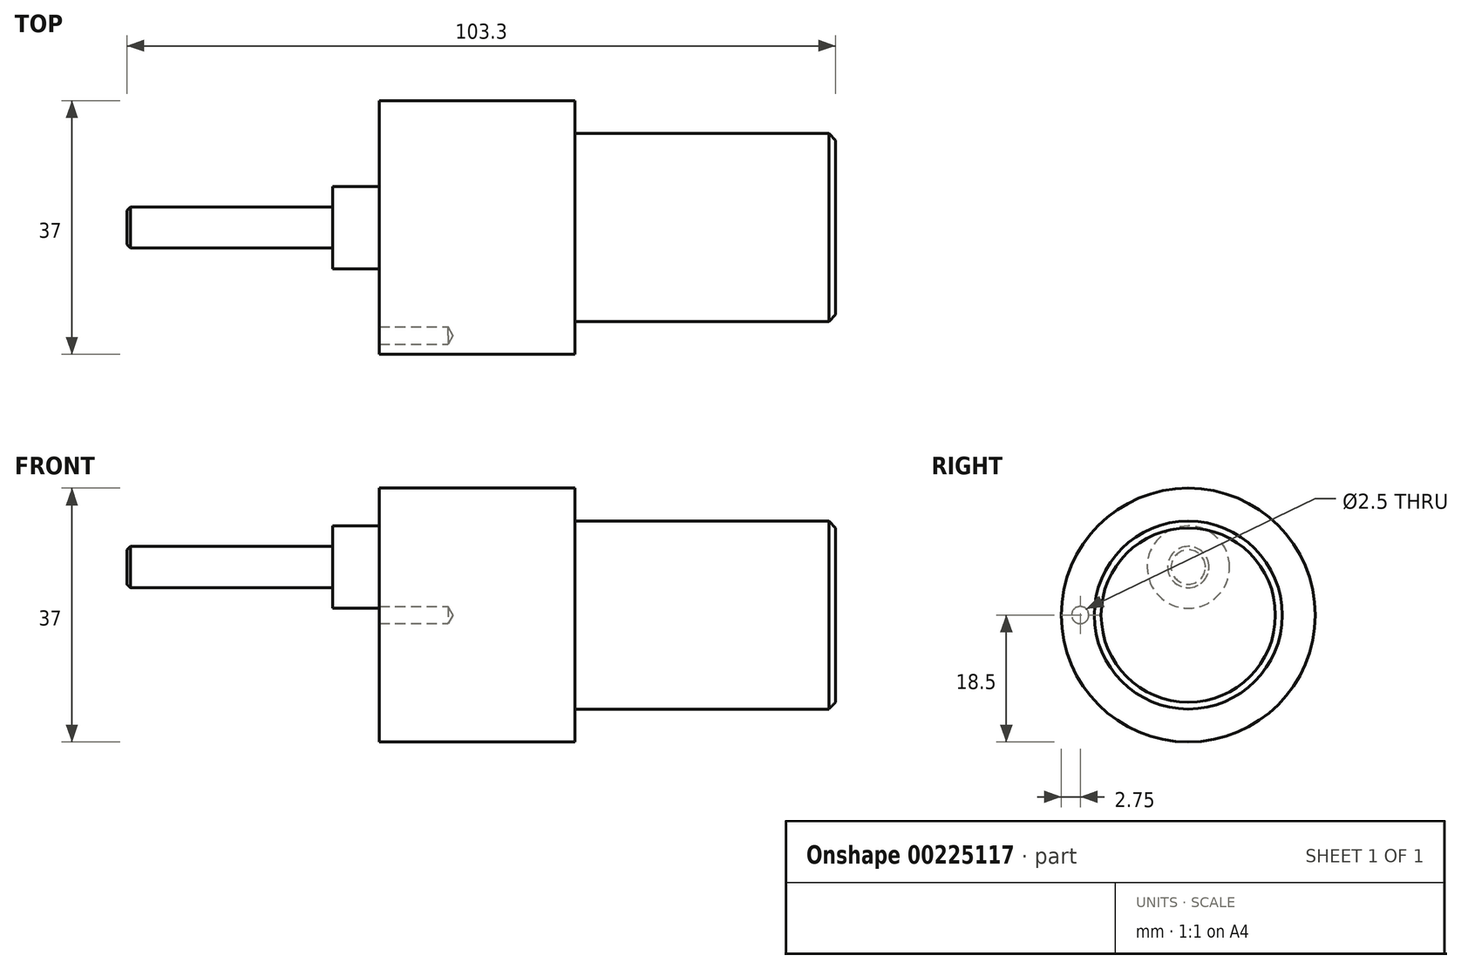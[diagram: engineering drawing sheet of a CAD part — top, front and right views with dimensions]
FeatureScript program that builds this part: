
annotation { "Feature Type Name" : "Feature", "Feature Type Description" : "" }
export const myFeature = defineFeature(function(context is Context, id is Id, definition is map)
    precondition{}
    {
        {
            var Q0;
            Q0=qCreatedBy(makeId("Front.planeOp"),FACE);
            var sketch = newSketch(context, id + "F0", { "sketchPlane" : qUnion([Q0])});
            skLineSegment(sketch, "E0", {"start": v(-36.39, 0) * mm, "end": v(44.16, 0) * mm, "construction": true});
            skLineSegment(sketch, "E1.bottom", {"start": v(-28.5, 0) * mm, "end": v(0, 0) * mm});
            skLineSegment(sketch, "E1.top", {"start": v(-28.5, 18.5) * mm, "end": v(0, 18.5) * mm});
            skLineSegment(sketch, "E1.left", {"start": v(-28.5, 0) * mm, "end": v(-28.5, 18.5) * mm});
            skLineSegment(sketch, "E1.right", {"start": v(0, 0) * mm, "end": v(0, 18.5) * mm});
            skLineSegment(sketch, "E2.bottom", {"start": v(0, 13.7) * mm, "end": v(38, 13.7) * mm});
            skLineSegment(sketch, "E2.top", {"start": v(0, 0) * mm, "end": v(38, 0) * mm});
            skLineSegment(sketch, "E2.left", {"start": v(0, 13.7) * mm, "end": v(0, 0) * mm});
            skLineSegment(sketch, "E2.right", {"start": v(38, 13.7) * mm, "end": v(38, 0) * mm});
            skLineSegment(sketch, "E3.left", {"start": v(-28.5, 13) * mm, "end": v(-28.5, 1) * mm});
            skLineSegment(sketch, "E3.right", {"start": v(-35.3, 13) * mm, "end": v(-35.3, 10) * mm});
            skLineSegment(sketch, "E4.bottom", {"start": v(-65.3, 10) * mm, "end": v(-35.3, 10) * mm});
            skLineSegment(sketch, "E4.left", {"start": v(-65.3, 10) * mm, "end": v(-65.3, 7) * mm});
            skLineSegment(sketch, "E5", {"start": v(-65.3, 7) * mm, "end": v(-28.5, 7) * mm});
            skPoint(sketch, "E4.top.start.orphan", {"position": v(-65.3, 4) * mm});
            skLineSegment(sketch, "E6", {"start": v(-35.3, 13) * mm, "end": v(-28.5, 13) * mm});
            skSolve(sketch);
        }
        {
            var Q0;
            {var subQ3=sQuery(id+"F0.wireOp",EDGE,"E1.bottom");Q0=makeQuery(id+"F0.imprint","IMPRINT",FACE,{"disambiguationData":[TD([[makeQuery(id+"F0.imprint","IMPRINT",EDGE,{"derivedFrom":subQ3}),1.0]])]});}
            var Q1;
            Q1=makeQuery(id+"F0.imprint","IMPRINT",FACE,{"disambiguationData":[TD([[makeQuery(id+"F0.imprint","IMPRINT",EDGE,{"derivedFrom":sQuery(id+"F0.wireOp",EDGE,"E2.bottom")}),-1.0]])]});
            var Q2;
            Q2=sQuery(id+"F0.wireOp",EDGE,"E0");
            revolve(context, id + "F1", {"entities" : qUnion([Q0, Q1]), "axis" : qUnion([Q2]), "revolveType" : RevolveType.FULL});
        }
        {
            var Q0;
            Q0=makeQuery(id+"F0.imprint","IMPRINT",FACE,{"disambiguationData":[TD([[makeQuery(id+"F0.imprint","IMPRINT",EDGE,{"derivedFrom":sQuery(id+"F0.wireOp",EDGE,"E3.right")}),1.0]])]});
            var Q1;
            Q1=sQuery(id+"F0.wireOp",EDGE,"E5");
            revolve(context, id + "F2", {"operationType" : NewBodyOperationType.ADD, "entities" : qUnion([Q0]), "axis" : qUnion([Q1]), "revolveType" : RevolveType.FULL});
        }
        {
            var Q0;
            Q0=makeQuery(id+"F2.opRevolve","SWEPT_EDGE",EDGE,{"disambiguationData":[OSD([sQuery(id+"F0.wireOp",EDGE,"E4.bottom"),sQuery(id+"F0.wireOp",EDGE,"E4.left")])]});
            chamfer(context, id + "F3", {"entities" : qUnion([Q0]), "width" : 0.5 * mm, "tangentPropagation" : true});
        }
        {
            var Q0;
            Q0=makeQuery(id+"F1.opRevolve","SWEPT_FACE",FACE,{"disambiguationData":[OSD([sQuery(id+"F0.wireOp",EDGE,"E1.left"),sQuery(id+"F0.wireOp",EDGE,"E3.left")])]});
            var sketch = newSketch(context, id + "F4", { "sketchPlane" : qUnion([Q0])});
            skCircle(sketch, "E7", {"center": v(0, 0) * mm, "radius": 15.75 * mm, "construction": true});
            skCircle(sketch, "E8", {"center": v(15.75, 0) * mm, "radius": 1.5 * mm});
            skSolve(sketch);
        }
        {
            var Q0;
            Q0=sQuery(id+"F4.wireOp",VERTEX,"E8.center");
            var Q1;
            Q1=makeQuery(id+"F1.opRevolve","SWEPT_BODY",BODY,{"disambiguationData":[OSD([sQuery(id+"F0.wireOp",EDGE,"E1.bottom"),sQuery(id+"F0.wireOp",EDGE,"E1.top"),sQuery(id+"F0.wireOp",EDGE,"E1.left"),sQuery(id+"F0.wireOp",EDGE,"E1.right"),sQuery(id+"F0.wireOp",EDGE,"E2.bottom"),sQuery(id+"F0.wireOp",EDGE,"E2.top"),sQuery(id+"F0.wireOp",EDGE,"E2.right"),sQuery(id+"F0.wireOp",EDGE,"E3.left")])]});
            hole(context, id + "F5", {"style" : HoleStyle.SIMPLE, "endStyle" : HoleEndStyle.BLIND, "standardTappedOrClearance" : lookupTablePath({ "standard" : "ISO", "engagement" : "75%", "pitch" : "0.5 mm", "size" : "M3", "type" : "Tapped" }), "standardBlindInLast" : lookupTablePath({ "standard" : "ISO", "engagement" : "75%", "pitch" : "0.5 mm", "size" : "M3", "type" : "Tapped" }), "holeDiameter" : 2.5 * mm, "holeDepth" : 10 * mm, "locations" : qUnion([Q0]), "scope" : qUnion([Q1]), "majorDiameter" : 3 * mm, "startStyle" : HoleStartStyle.SKETCH});
        }
        {
            var Q0;
            Q0=makeQuery(id+"F1.opRevolve","SWEPT_EDGE",EDGE,{"disambiguationData":[OSD([sQuery(id+"F0.wireOp",EDGE,"E2.bottom"),sQuery(id+"F0.wireOp",EDGE,"E2.right")])]});
            chamfer(context, id + "F6", {"entities" : qUnion([Q0]), "width" : 1 * mm, "tangentPropagation" : true});
        }
    });
